# Revit family: Legrand Benelux Snap on Mobile Columns
name_source: partatom
category: Installations électriques
units: mm (PartAtom-declared; Revit-internal decimal feet)

## family parameters
Basée sur le plan de construction = Non
Conserver l'orientation des annotations = Non
Cote de connecteur circulaire = Utiliser le diamètre
Couper avec des vides une fois chargée = Non
Partagée = Non
Point de calcul de pièce = Non
Toujours verticalement = Oui
Type d'élément = Normal

## types (6) — shared parameters
Fabricant = LEGRAND
Main Material = Aluminum
Standard = Snap-on-ON
zero-valued in all types: Elévation par défaut

## per-type parameters (varying)
| type | Column Stand type | Column type | Description | Finishing | Modèle | Number of compartments | Offset | not Black |
| Movable Column  1 cpt 45 2M White | Movable feet : Foot for mini Column White | Column - SNAP-ON : Movable Column  1 cpt 45 2M White | White Movable Column  1comp. cover45 2 m with 1 foot and flexib. ovaline 1m radius | White | LG-653006 | 1 compartment | 10 mm  [stored 0.0328084 ft] | Oui |
| Movable Column  1 cpt CV45 2M Alu | Movable feet : Foot for mini Column Alu | Column - SNAP-ON : Movable Column  1 cpt CV45 2M Alu | Alum. Movable Column  1comp. cover45 2 m with 1 foot and flexib. ovaline 1m radius | Aluminum | LG-653007 | 1 compartment | 10 mm  [stored 0.0328084 ft] | Oui |
| Movable Column  1 cpt 45 2M Black | Movable feet : Foot for mini Column White | Column - SNAP-ON : Movable Column  1 cpt CV45 2M Alu | Black Movable Column  1comp. cover45 2 m with 1 foot and flexib. ovaline 1m radius | Black | LG-653008 | 1 compartment | 0 mm  [stored 0 ft] | Non |
| Movable Column 2 cpt CV45 2M White | Movable feet : Foot for mini Column White | Column - SNAP-ON : Movable Column 2 cpt CV45 2M White | White Movable Column  2 comp. cover45 2 m with 1 foot and flexib. ovaline 1m radius | White | LG-653026 | 2 compartments | 10 mm  [stored 0.0328084 ft] | Oui |
| Movable Column 2 cpt CV45 2M Alu | Movable feet : Foot for mini Column Alu | Column - SNAP-ON : Movable Column 2 cpt CV45 2M Alu | Alum. Movable Column  2 comp. cover45 2 m with 1 foot and flexib. ovaline 1m radius | Aluminum | LG-653027 | 2 compartments | 10 mm  [stored 0.0328084 ft] | Oui |
| Movable Column 2 cpt CV45 2M Black | Movable feet : Foot for mini Column White | Column - SNAP-ON : Movable Column 2 cpt CV45 2M Black | Black Movable Column  2 comp. cover45 2 m with 1 foot and flexib. ovaline 1m radius | Black | LG-653028 | 2 compartments | 0 mm  [stored 0 ft] | Non |

note: [stored X ft] marks values corroborated as IEEE doubles in the binary element streams (Revit-internal decimal feet)
